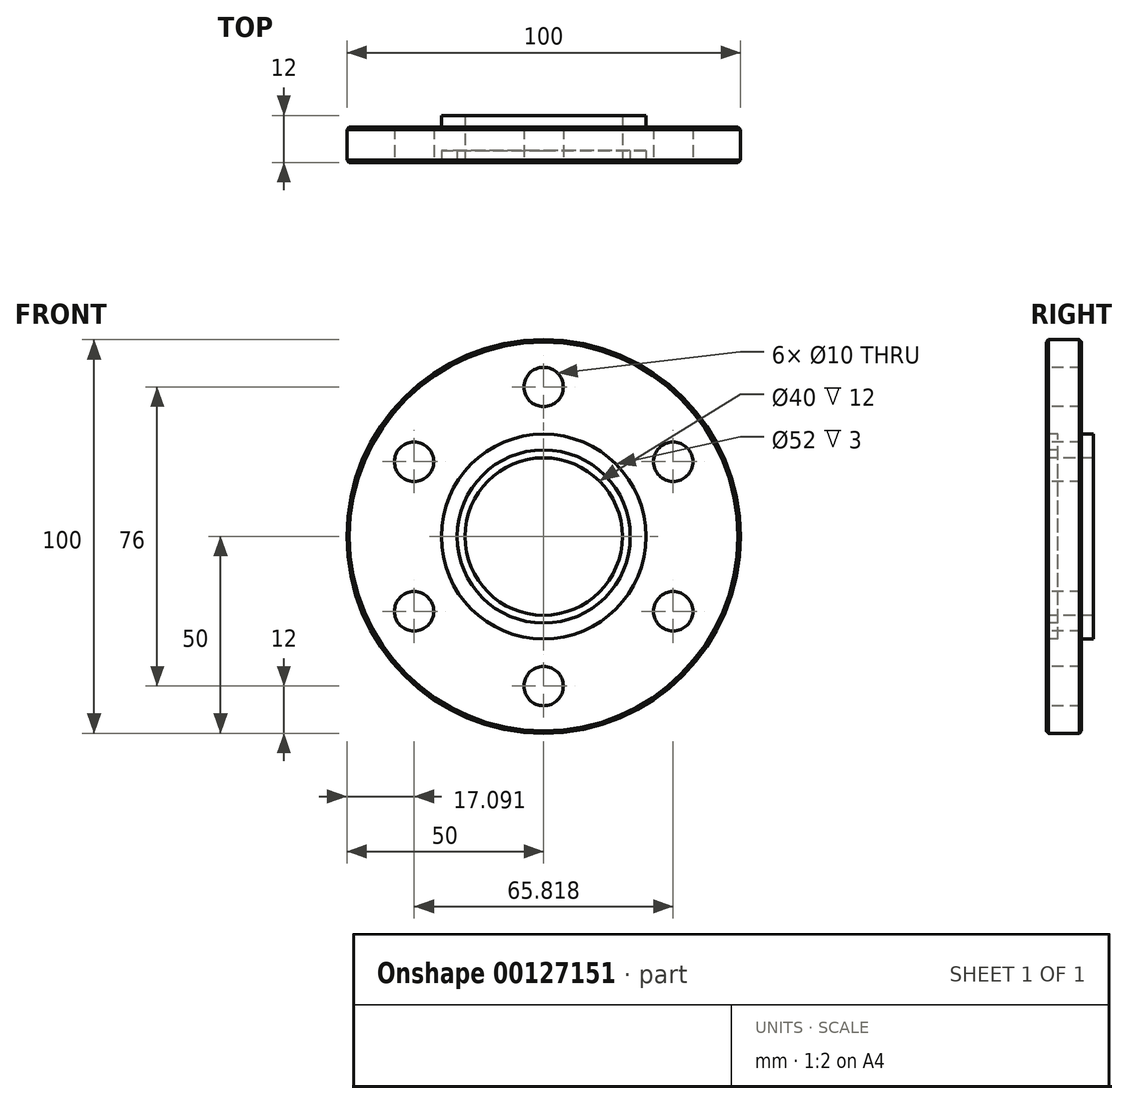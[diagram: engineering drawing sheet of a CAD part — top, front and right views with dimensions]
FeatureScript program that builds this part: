
annotation { "Feature Type Name" : "Feature", "Feature Type Description" : "" }
export const myFeature = defineFeature(function(context is Context, id is Id, definition is map)
    precondition{}
    {
        {
            var Q0;
            Q0=qCreatedBy(makeId("Front.planeOp"),FACE);
            var sketch = newSketch(context, id + "F0", { "sketchPlane" : qUnion([Q0])});
            skCircle(sketch, "E0", {"center": v(0, 0) * mm, "radius": 50 * mm});
            skLineSegment(sketch, "E1", {"start": v(0, 0) * mm, "end": v(0, 50) * mm, "construction": true});
            skLineSegment(sketch, "E2", {"start": v(0, 0) * mm, "end": v(0, -50) * mm, "construction": true});
            skCircle(sketch, "E3", {"center": v(0, 38) * mm, "radius": 5 * mm});
            skCircle(sketch, "E4.1.0", {"center": v(-32.9, 19) * mm, "radius": 5 * mm});
            skCircle(sketch, "E4.2.0", {"center": v(-32.9, -19) * mm, "radius": 5 * mm});
            skCircle(sketch, "E4.3.0", {"center": v(0, -38) * mm, "radius": 5 * mm});
            skCircle(sketch, "E4.4.0", {"center": v(32.9, -19) * mm, "radius": 5 * mm});
            skCircle(sketch, "E4.5.0", {"center": v(32.9, 19) * mm, "radius": 5 * mm});
            skCircle(sketch, "E5", {"center": v(0, 0) * mm, "radius": 26 * mm});
            skCircle(sketch, "E6", {"center": v(0, 0) * mm, "radius": 22 * mm});
            skCircle(sketch, "E7", {"center": v(0, 0) * mm, "radius": 20 * mm});
            skSolve(sketch);
        }
        {
            var Q0;
            Q0=makeQuery(id+"F0.imprint","IMPRINT",FACE,{"disambiguationData":[TD([[makeQuery(id+"F0.imprint","IMPRINT",EDGE,{"derivedFrom":sQuery(id+"F0.wireOp",EDGE,"E0")}),1.0]])]});
            var Q1;
            Q1=makeQuery(id+"F0.imprint","IMPRINT",FACE,{"disambiguationData":[TD([[makeQuery(id+"F0.imprint","IMPRINT",EDGE,{"derivedFrom":sQuery(id+"F0.wireOp",EDGE,"E5")}),1.0]])]});
            var Q2;
            Q2=makeQuery(id+"F0.imprint","IMPRINT",FACE,{"disambiguationData":[TD([[makeQuery(id+"F0.imprint","IMPRINT",EDGE,{"derivedFrom":sQuery(id+"F0.wireOp",EDGE,"E6")}),1.0]])]});
            extrude(context, id + "F1", {"entities" : qUnion([Q0, Q1, Q2]), "endBound" : BoundingType.SYMMETRIC, "oppositeDirection" : true, "depth" : 12 * mm});
        }
        {
            var Q0;
            Q0=makeQuery(id+"F1.opExtrude","CAP_FACE",FACE,{"disambiguationData":[OSD([sQuery(id+"F0.wireOp",EDGE,"E0"),sQuery(id+"F0.wireOp",EDGE,"E3"),sQuery(id+"F0.wireOp",EDGE,"E4.1.0"),sQuery(id+"F0.wireOp",EDGE,"E4.2.0"),sQuery(id+"F0.wireOp",EDGE,"E4.3.0"),sQuery(id+"F0.wireOp",EDGE,"E4.4.0"),sQuery(id+"F0.wireOp",EDGE,"E4.5.0"),sQuery(id+"F0.wireOp",EDGE,"E7")])],"isStart":true});
            var sketch = newSketch(context, id + "F2", { "sketchPlane" : qUnion([Q0])});
            skCircle(sketch, "E8.0", {"center": v(0, 0) * mm, "radius": 26 * mm});
            skCircle(sketch, "E8.1", {"center": v(0, 0) * mm, "radius": 22 * mm});
            skSolve(sketch);
        }
        {
            var Q0;
            Q0=makeQuery(id+"F2.imprint","IMPRINT",FACE,{"disambiguationData":[TD([[makeQuery(id+"F2.imprint","IMPRINT",EDGE,{"derivedFrom":sQuery(id+"F2.wireOp",EDGE,"E8.0")}),1.0]])]});
            extrude(context, id + "F3", {"entities" : qUnion([Q0]), "operationType" : NewBodyOperationType.REMOVE, "oppositeDirection" : true, "depth" : 3 * mm});
        }
        {
            var Q0;
            Q0=makeQuery(id+"F1.opExtrude","CAP_FACE",FACE,{"disambiguationData":[OSD([sQuery(id+"F0.wireOp",EDGE,"E0"),sQuery(id+"F0.wireOp",EDGE,"E3"),sQuery(id+"F0.wireOp",EDGE,"E4.1.0"),sQuery(id+"F0.wireOp",EDGE,"E4.2.0"),sQuery(id+"F0.wireOp",EDGE,"E4.3.0"),sQuery(id+"F0.wireOp",EDGE,"E4.4.0"),sQuery(id+"F0.wireOp",EDGE,"E4.5.0"),sQuery(id+"F0.wireOp",EDGE,"E7")])],"isStart":false});
            var sketch = newSketch(context, id + "F4", { "sketchPlane" : qUnion([Q0])});
            skSolve(sketch);
        }
        {
            var Q0;
            Q0=makeQuery(id+"F4.imprint","IMPRINT",FACE,{"disambiguationData":[TD([[makeQuery(id+"F4.imprint","IMPRINT",EDGE,{"derivedFrom":makeQuery(id+"F1.opExtrude","CAP_EDGE",EDGE,{"disambiguationData":[OSD([sQuery(id+"F0.wireOp",EDGE,"E0")])],"isStart":false})}),-1.0]])]});
            var sketch = newSketch(context, id + "F5", { "sketchPlane" : qUnion([Q0])});
            skCircle(sketch, "E9.0", {"center": v(0, 0) * mm, "radius": 26 * mm});
            skCircle(sketch, "E9.1", {"center": v(0, 0) * mm, "radius": 22 * mm});
            skSolve(sketch);
        }
        {
            var Q0;
            Q0=makeQuery(id+"F5.imprint","IMPRINT",FACE,{"disambiguationData":[TD([[makeQuery(id+"F5.imprint","IMPRINT",EDGE,{"derivedFrom":sQuery(id+"F5.wireOp",EDGE,"E9.0")}),-1.0]])]});
            extrude(context, id + "F6", {"entities" : qUnion([Q0]), "operationType" : NewBodyOperationType.REMOVE, "oppositeDirection" : true, "depth" : 3 * mm});
        }
        {
            var Q0;
            Q0=makeQuery(id+"F1.opExtrude","SWEPT_FACE",FACE,{"disambiguationData":[OSD([sQuery(id+"F0.wireOp",EDGE,"E0")])]});
            chamfer(context, id + "F7", {"entities" : qUnion([Q0]), "width" : .6 * mm, "tangentPropagation" : true});
        }
    });
